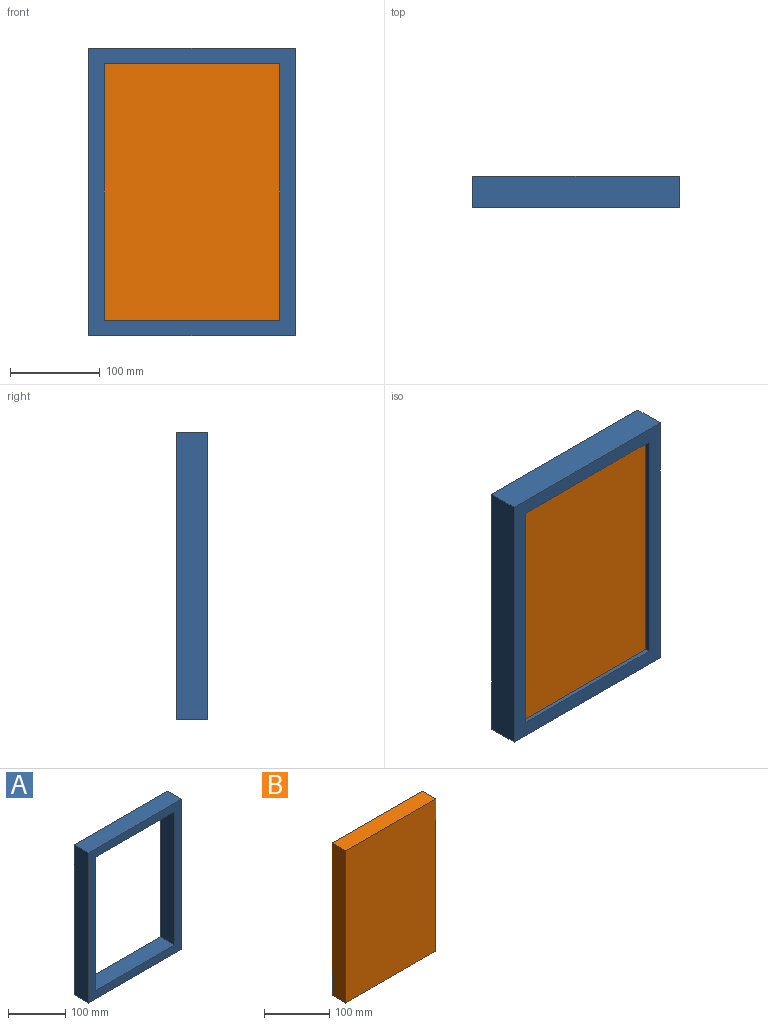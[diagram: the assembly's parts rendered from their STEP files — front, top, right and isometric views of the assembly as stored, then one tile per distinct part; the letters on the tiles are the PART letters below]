
ASSEMBLY  parts=2 mates=1
PART A: 10 faces, bbox 230x35x320 mm
  f0: plane 230x35mm, normal (0,0,-1), area 8050mm2, adj f1,f7,f8,f9
  f1: plane 320x35mm, normal (1,0,0), area 11200mm2, adj f0,f2,f8,f9
  f2: plane 230x35mm, normal (0,0,1), area 8050mm2, adj f1,f7,f8,f9
  f3: plane 195x35mm, normal (0,0,-1), area 6825mm2, adj f4,f6,f8,f9
  f4: plane 285x35mm, normal (-1,0,0), area 9975mm2, adj f3,f5,f8,f9
  f5: plane 195x35mm, normal (0,0,1), area 6825mm2, adj f4,f6,f8,f9
  f6: plane 285x35mm, normal (1,0,0), area 9975mm2, adj f3,f5,f8,f9
  f7: plane 320x35mm, normal (-1,0,0), area 11200mm2, adj f0,f2,f8,f9
  f8: plane 320x230mm, normal (0,-1,0), area 18025mm2, adj f0,f1,f2,f3,f4,f5,f6,f7
  f9: plane 320x230mm, normal (0,1,0), area 18025mm2, adj f0,f1,f2,f3,f4,f5,f6,f7
PART B: 6 faces, bbox 195x30x285 mm
  f0: plane 285x30mm, normal (1,0,0), area 8550mm2, adj f1,f3,f4,f5
  f1: plane 195x30mm, normal (0,0,1), area 5850mm2, adj f0,f2,f4,f5
  f2: plane 285x30mm, normal (-1,0,0), area 8550mm2, adj f1,f3,f4,f5
  f3: plane 195x30mm, normal (0,0,-1), area 5850mm2, adj f0,f2,f4,f5
  f4: plane 285x195mm, normal (0,-1,0), area 55575mm2, adj f0,f1,f2,f3
  f5: plane 285x195mm, normal (0,1,0), area 55575mm2, adj f0,f1,f2,f3
PLACE A t=(0,35,0)mm
PLACE B t=(0,35,0)mm
MATE fastened B.f5 <-> A.f9  axis (0,1,0) through (97.5,35,-142.5)mm
